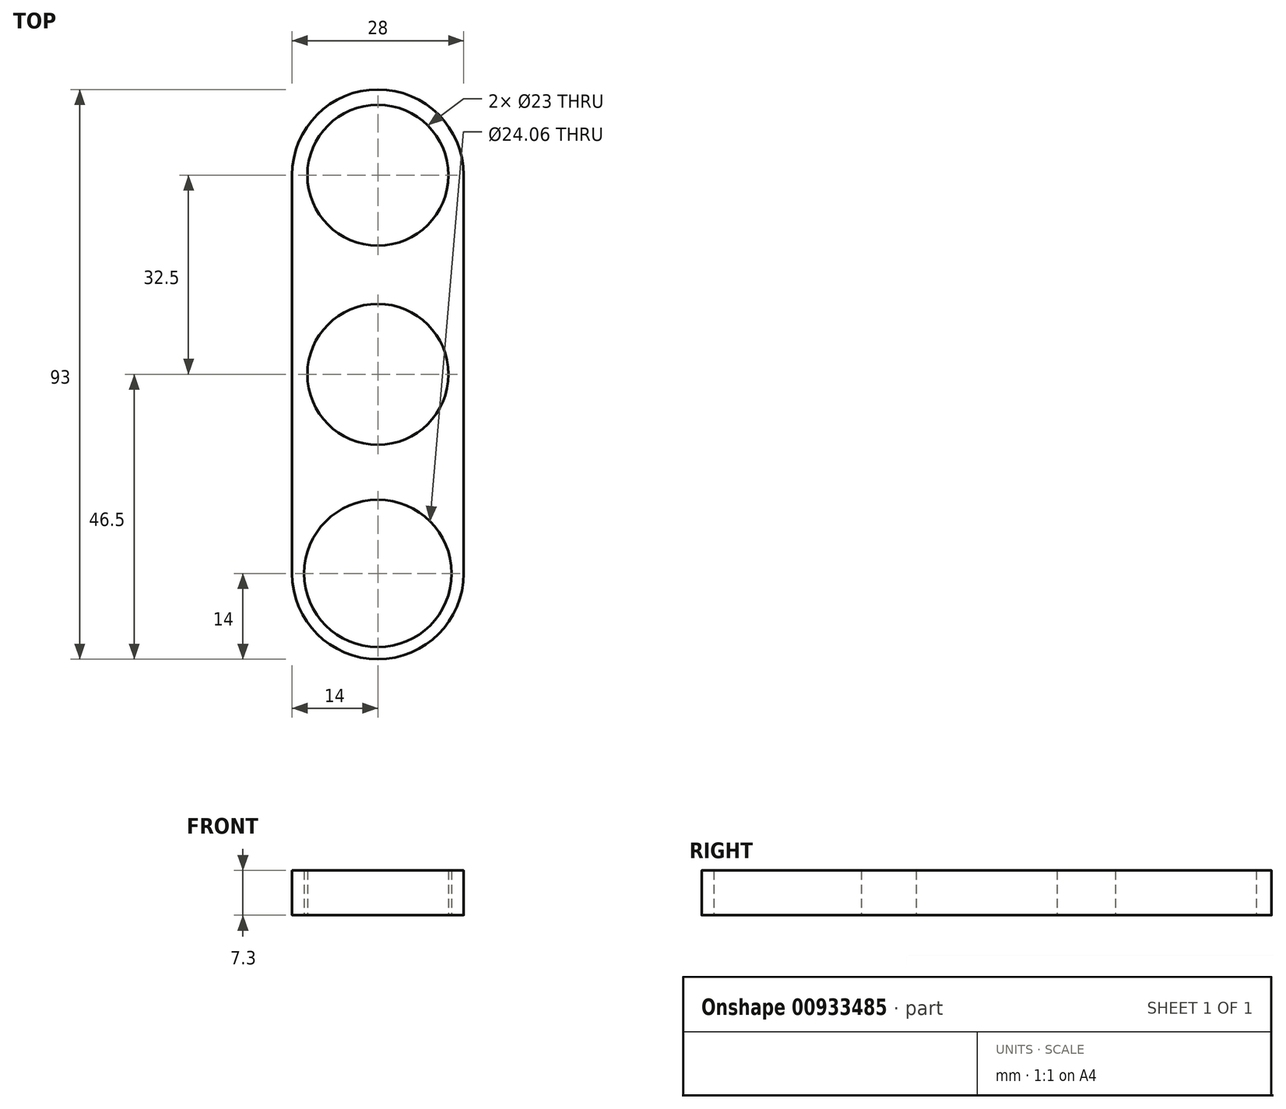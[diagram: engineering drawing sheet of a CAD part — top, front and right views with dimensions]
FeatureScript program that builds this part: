
annotation { "Feature Type Name" : "Feature", "Feature Type Description" : "" }
export const myFeature = defineFeature(function(context is Context, id is Id, definition is map)
    precondition{}
    {
        {
            var Q0;
            Q0=qCreatedBy(makeId("Top.planeOp"),FACE);
            var sketch = newSketch(context, id + "F0", { "sketchPlane" : qUnion([Q0])});
            skCircle(sketch, "E0", {"center": v(0, 0) * mm, "radius": 11.5 * mm});
            skLineSegment(sketch, "E1", {"start": v(0, 44) * mm, "end": v(0, 46.5) * mm});
            skLineSegment(sketch, "E2", {"start": v(0, 0) * mm, "end": v(-11.5, 0) * mm});
            skCircle(sketch, "E3", {"center": v(0, 32.5) * mm, "radius": 11.5 * mm});
            skCircle(sketch, "E4", {"center": v(0, -32.5) * mm, "radius": 12.03 * mm});
            skLineSegment(sketch, "E5", {"start": v(-12.03, -32.5) * mm, "end": v(-12.03, -32.3) * mm});
            skLineSegment(sketch, "E6", {"start": v(0, -32.5) * mm, "end": v(12.03, -32.5) * mm});
            skArc(sketch, "E7", {"start": v(14, 32.5) * mm, "mid": v(0, 46.5) * mm, "end": v(-14, 32.5) * mm});
            skArc(sketch, "E8", {"start": v(-14, -32.5) * mm, "mid": v(0, -46.5) * mm, "end": v(14, -32.5) * mm});
            skLineSegment(sketch, "E9", {"start": v(-14, -32.5) * mm, "end": v(-12.03, -32.5) * mm});
            skLineSegment(sketch, "E10", {"start": v(14, 32.5) * mm, "end": v(14, -32.5) * mm});
            skLineSegment(sketch, "E11", {"start": v(-14, -32.5) * mm, "end": v(-14, 32.5) * mm});
            skLineSegment(sketch, "E12.trimOffspring", {"start": v(12.03, -32.3) * mm, "end": v(12.03, -32.5) * mm});
            skPoint(sketch, "E13.end.orphan", {"position": v(-11.5, 32.5) * mm});
            skPoint(sketch, "E14.orphan", {"position": v(0, 65) * mm});
            skPoint(sketch, "E15.orphan", {"position": v(0, -65) * mm});
            skLineSegment(sketch, "E16.trimOffspring", {"start": v(0, -44.53) * mm, "end": v(0, -46.5) * mm});
            skSolve(sketch);
        }
        {
            var Q0;
            Q0 = qSketchRegion(id + "F0", true);
            extrude(context, id + "F1", {"entities" : qUnion([Q0]), "depth" : 7.3 * mm, "offsetDistance" : 25 * mm});
        }
        {
            var Q0;
            Q0=makeQuery(id+"F1.opExtrude","CAP_EDGE",EDGE,{"disambiguationData":[OSD([sQuery(id+"F0.wireOp",EDGE,"E7")])],"isStart":false});
            var Q1;
            Q1=makeQuery(id+"F1.opExtrude","CAP_EDGE",EDGE,{"disambiguationData":[OSD([sQuery(id+"F0.wireOp",EDGE,"E11")])],"isStart":false});
            var Q2;
            Q2=makeQuery(id+"F1.opExtrude","CAP_EDGE",EDGE,{"disambiguationData":[OSD([sQuery(id+"F0.wireOp",EDGE,"E8")])],"isStart":false});
            var Q3;
            Q3=makeQuery(id+"F1.opExtrude","CAP_EDGE",EDGE,{"disambiguationData":[OSD([sQuery(id+"F0.wireOp",EDGE,"E10")])],"isStart":false});
            var Q4;
            Q4=makeQuery(id+"F1.opExtrude","CAP_EDGE",EDGE,{"disambiguationData":[OSD([sQuery(id+"F0.wireOp",EDGE,"E7")])],"isStart":true});
            var Q5;
            Q5=makeQuery(id+"F1.opExtrude","CAP_EDGE",EDGE,{"disambiguationData":[OSD([sQuery(id+"F0.wireOp",EDGE,"E10")])],"isStart":true});
            var Q6;
            Q6=makeQuery(id+"F1.opExtrude","CAP_EDGE",EDGE,{"disambiguationData":[OSD([sQuery(id+"F0.wireOp",EDGE,"E11")])],"isStart":true});
            var Q7;
            Q7=makeQuery(id+"F1.opExtrude","CAP_EDGE",EDGE,{"disambiguationData":[OSD([sQuery(id+"F0.wireOp",EDGE,"E8")])],"isStart":true});
            fillet(context, id + "F2", {"entities" : qUnion([Q0, Q1, Q2, Q3, Q4, Q5, Q6, Q7]), "radius" : 0.02 * mm, "tangentPropagation" : true, "allowEdgeOverflow" : false});
        }
    });
